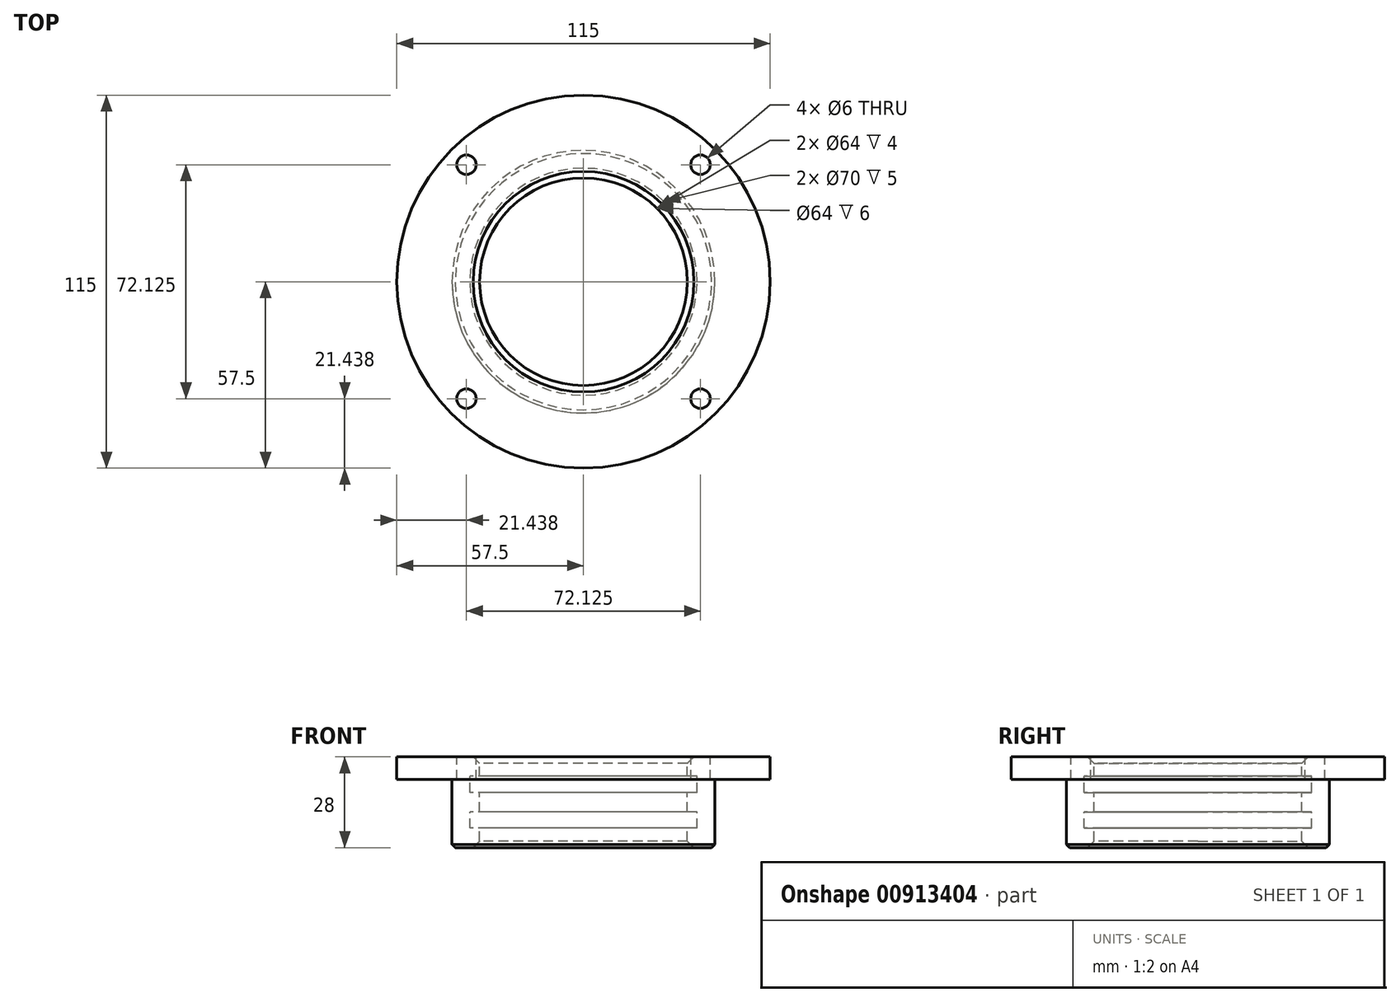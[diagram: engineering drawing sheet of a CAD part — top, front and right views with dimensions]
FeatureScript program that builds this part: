
annotation { "Feature Type Name" : "Feature", "Feature Type Description" : "" }
export const myFeature = defineFeature(function(context is Context, id is Id, definition is map)
    precondition{}
    {
        {
            var Q0;
            Q0=qCreatedBy(makeId("Front.planeOp"),FACE);
            var sketch = newSketch(context, id + "F0", { "sketchPlane" : qUnion([Q0])});
            skLineSegment(sketch, "E0", {"start": v(0, 122.59) * mm, "end": v(0, -130.63) * mm, "construction": true});
            skLineSegment(sketch, "E1", {"start": v(32, 0) * mm, "end": v(57.5, 0) * mm});
            skLineSegment(sketch, "E2", {"start": v(57.5, 0) * mm, "end": v(57.5, -7) * mm});
            skLineSegment(sketch, "E3", {"start": v(57.5, -7) * mm, "end": v(40.5, -7) * mm});
            skLineSegment(sketch, "E4", {"start": v(40.5, -7) * mm, "end": v(40.5, -28) * mm});
            skLineSegment(sketch, "E5", {"start": v(40.5, -28) * mm, "end": v(32, -28) * mm});
            skLineSegment(sketch, "E6", {"start": v(32, -28) * mm, "end": v(32, -22) * mm});
            skLineSegment(sketch, "E7", {"start": v(32, -22) * mm, "end": v(35, -22) * mm});
            skLineSegment(sketch, "E8", {"start": v(35, -22) * mm, "end": v(35, -17) * mm});
            skLineSegment(sketch, "E9", {"start": v(35, -17) * mm, "end": v(32, -17) * mm});
            skLineSegment(sketch, "E10", {"start": v(32, -17) * mm, "end": v(32, -11) * mm});
            skLineSegment(sketch, "E11", {"start": v(32, -11) * mm, "end": v(35, -11) * mm});
            skLineSegment(sketch, "E12", {"start": v(35, -11) * mm, "end": v(35, -6) * mm});
            skLineSegment(sketch, "E13", {"start": v(35, -6) * mm, "end": v(32, -6) * mm});
            skLineSegment(sketch, "E14", {"start": v(32, -6) * mm, "end": v(32, 0) * mm});
            skSolve(sketch);
        }
        {
            var Q0;
            Q0=makeQuery(id+"F0.imprint","IMPRINT",FACE,{"disambiguationData":[TD([[makeQuery(id+"F0.imprint","IMPRINT",EDGE,{"derivedFrom":sQuery(id+"F0.wireOp",EDGE,"E1")}),-1.0]])]});
            var Q1;
            Q1=sQuery(id+"F0.wireOp",EDGE,"E0");
            revolve(context, id + "F1", {"surfaceOperationType" : NewSurfaceOperationType.NEW, "entities" : qUnion([Q0]), "axis" : qUnion([Q1]), "revolveType" : RevolveType.FULL});
        }
        {
            var Q0;
            Q0=makeQuery(id+"F1.opRevolve","SWEPT_EDGE",EDGE,{"disambiguationData":[OSD([sQuery(id+"F0.wireOp",EDGE,"E1"),sQuery(id+"F0.wireOp",EDGE,"E14")])]});
            var Q1;
            Q1=makeQuery(id+"F1.opRevolve","SWEPT_EDGE",EDGE,{"disambiguationData":[OSD([sQuery(id+"F0.wireOp",EDGE,"E5"),sQuery(id+"F0.wireOp",EDGE,"E6")])]});
            chamfer(context, id + "F2", {"entities" : qUnion([Q0, Q1]), "width" : 2 * mm, "tangentPropagation" : true});
        }
        {
            var Q0;
            Q0=makeQuery(id+"F1.opRevolve","SWEPT_EDGE",EDGE,{"disambiguationData":[OSD([sQuery(id+"F0.wireOp",EDGE,"E4"),sQuery(id+"F0.wireOp",EDGE,"E5")])]});
            chamfer(context, id + "F3", {"entities" : qUnion([Q0]), "width" : 1 * mm, "tangentPropagation" : true});
        }
        {
            var Q0;
            Q0=makeQuery(id+"F1.opRevolve","SWEPT_FACE",FACE,{"disambiguationData":[OSD([sQuery(id+"F0.wireOp",EDGE,"E1")])]});
            var sketch = newSketch(context, id + "F4", { "sketchPlane" : qUnion([Q0])});
            skCircle(sketch, "E15", {"center": v(0, 0) * mm, "radius": 51 * mm, "construction": true});
            skLineSegment(sketch, "E16", {"start": v(65.11, 0) * mm, "end": v(0, 0) * mm, "construction": true});
            skLineSegment(sketch, "E17", {"start": v(0, 0) * mm, "end": v(47.1, 47.1) * mm, "construction": true});
            skCircle(sketch, "E18", {"center": v(36.06, 36.06) * mm, "radius": 3 * mm});
            skCircle(sketch, "E19.1.0", {"center": v(-36.06, 36.06) * mm, "radius": 3 * mm});
            skCircle(sketch, "E19.2.0", {"center": v(-36.06, -36.06) * mm, "radius": 3 * mm});
            skCircle(sketch, "E19.3.0", {"center": v(36.06, -36.06) * mm, "radius": 3 * mm});
            skSolve(sketch);
        }
        {
            var Q0;
            Q0=makeQuery(id+"F4.imprint","IMPRINT",FACE,{"disambiguationData":[TD([[makeQuery(id+"F4.imprint","IMPRINT",EDGE,{"derivedFrom":sQuery(id+"F4.wireOp",EDGE,"E19.1.0")}),1.0]])]});
            var Q1;
            Q1=makeQuery(id+"F4.imprint","IMPRINT",FACE,{"disambiguationData":[TD([[makeQuery(id+"F4.imprint","IMPRINT",EDGE,{"derivedFrom":sQuery(id+"F4.wireOp",EDGE,"E18")}),1.0]])]});
            var Q2;
            Q2=makeQuery(id+"F4.imprint","IMPRINT",FACE,{"disambiguationData":[TD([[makeQuery(id+"F4.imprint","IMPRINT",EDGE,{"derivedFrom":sQuery(id+"F4.wireOp",EDGE,"E19.3.0")}),1.0]])]});
            var Q3;
            Q3=makeQuery(id+"F4.imprint","IMPRINT",FACE,{"disambiguationData":[TD([[makeQuery(id+"F4.imprint","IMPRINT",EDGE,{"derivedFrom":sQuery(id+"F4.wireOp",EDGE,"E19.2.0")}),1.0]])]});
            extrude(context, id + "F5", {"entities" : qUnion([Q0, Q1, Q2, Q3]), "operationType" : NewBodyOperationType.REMOVE, "oppositeDirection" : true, "depth" : 25 * mm, "offsetDistance" : 25 * mm});
        }
    });
